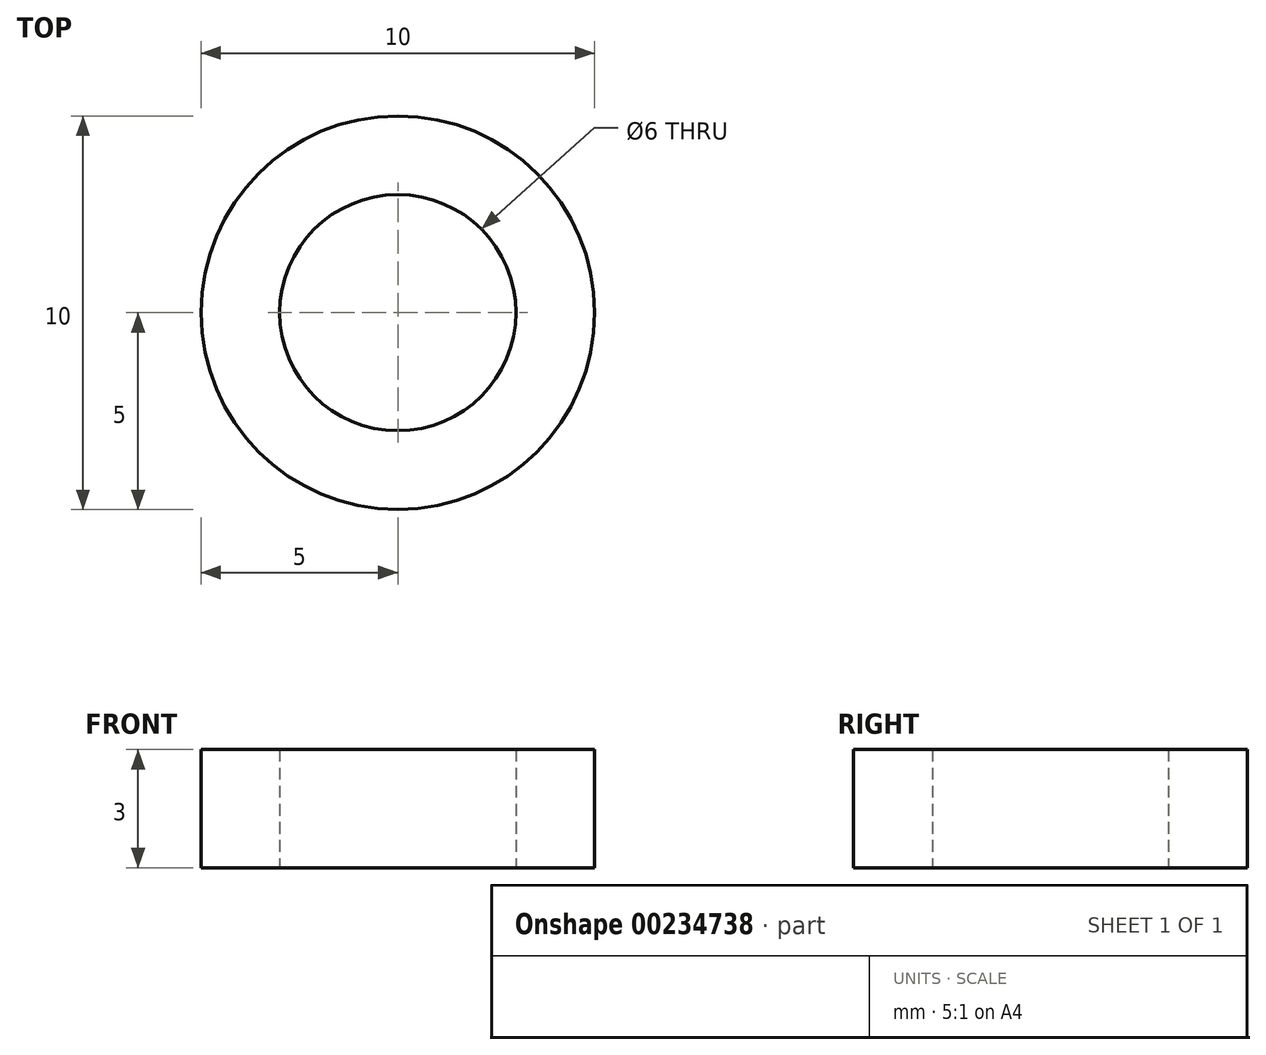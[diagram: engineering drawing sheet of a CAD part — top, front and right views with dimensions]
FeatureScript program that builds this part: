
annotation { "Feature Type Name" : "Feature", "Feature Type Description" : "" }
export const myFeature = defineFeature(function(context is Context, id is Id, definition is map)
    precondition{}
    {
        {
            var Q0;
            Q0=qCreatedBy(makeId("Top.planeOp"),FACE);
            var sketch = newSketch(context, id + "F0", { "sketchPlane" : qUnion([Q0])});
            skCircle(sketch, "E0", {"center": v(0, 0) * mm, "radius": 5 * mm});
            skCircle(sketch, "E1", {"center": v(0, 0) * mm, "radius": 3 * mm});
            skSolve(sketch);
        }
        {
            var Q0;
            Q0 = qSketchRegion(id + "F0", true);
            extrude(context, id + "F1", {"entities" : qUnion([Q0]), "endBound" : BoundingType.SYMMETRIC, "depth" : 3 * mm});
        }
    });
